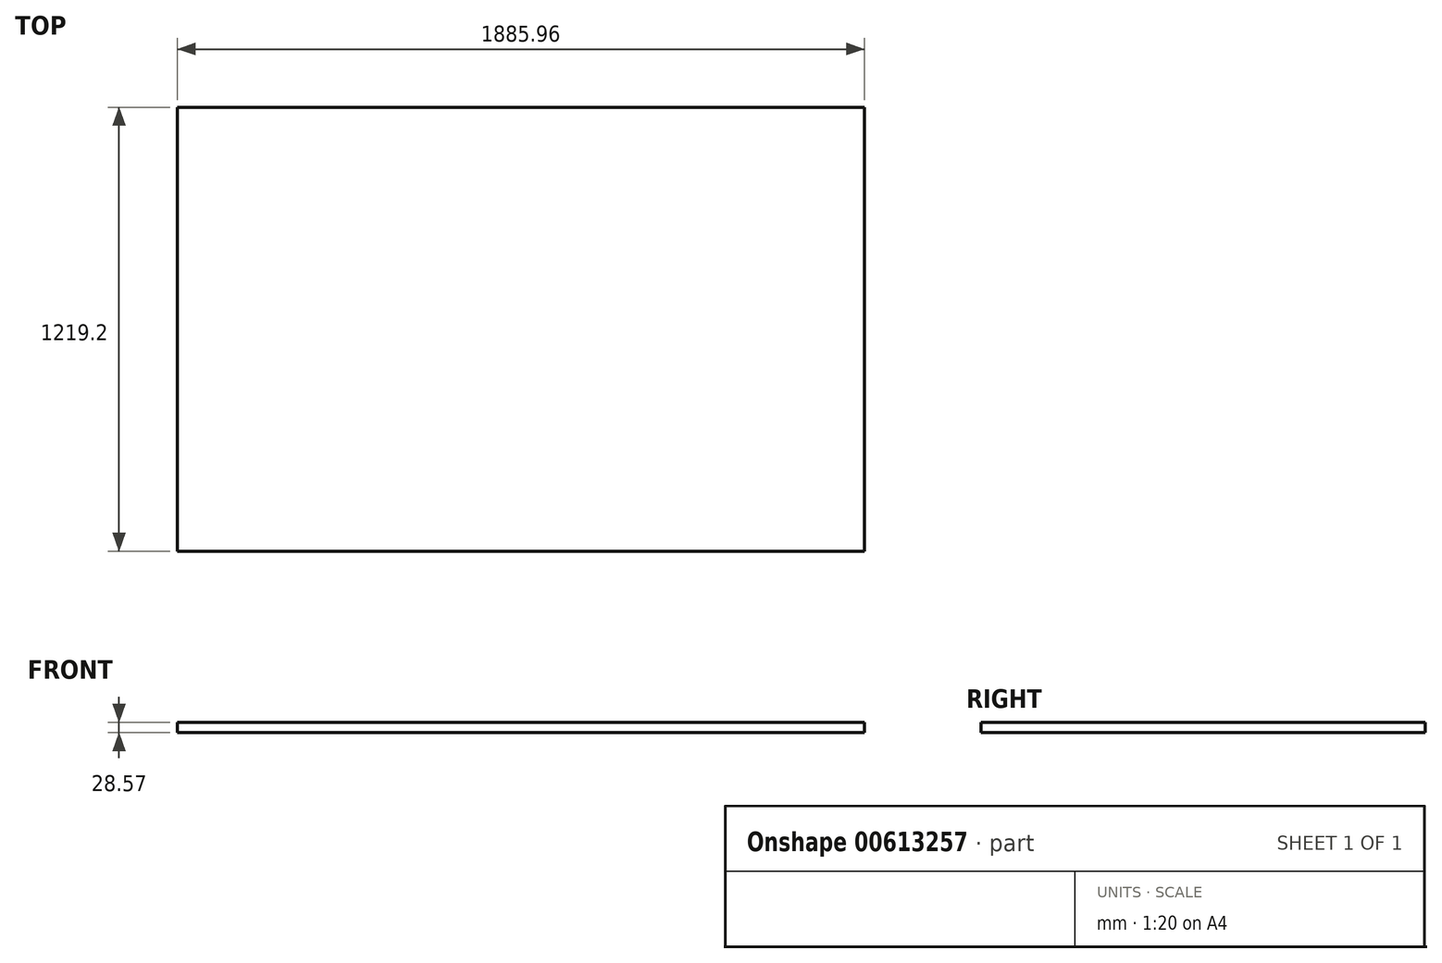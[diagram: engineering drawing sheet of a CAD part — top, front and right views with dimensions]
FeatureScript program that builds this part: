
annotation { "Feature Type Name" : "Feature", "Feature Type Description" : "" }
export const myFeature = defineFeature(function(context is Context, id is Id, definition is map)
    precondition{}
    {
        {
            var Q0;
            Q0=qCreatedBy(makeId("Top.planeOp"),FACE);
            var sketch = newSketch(context, id + "F0", { "sketchPlane" : qUnion([Q0])});
            skLineSegment(sketch, "E0.bottom", {"start": v(942.98, 609.6) * mm, "end": v(-942.98, 609.6) * mm});
            skLineSegment(sketch, "E0.top", {"start": v(942.98, -609.6) * mm, "end": v(-942.98, -609.6) * mm});
            skLineSegment(sketch, "E0.left", {"start": v(942.98, 609.6) * mm, "end": v(942.98, -609.6) * mm});
            skLineSegment(sketch, "E0.right", {"start": v(-942.98, 609.6) * mm, "end": v(-942.98, -609.6) * mm});
            skPoint(sketch, "E0.middle", {"position": v(0, 0) * mm});
            skSolve(sketch);
        }
        {
            var Q0;
            Q0=makeQuery(id+"F0.imprint","IMPRINT",FACE,{"disambiguationData":[TD([[makeQuery(id+"F0.imprint","IMPRINT",EDGE,{"derivedFrom":sQuery(id+"F0.wireOp",EDGE,"E0.bottom")}),1.0]])]});
            extrude(context, id + "F1", {"entities" : qUnion([Q0]), "depth" : 28.57 * mm, "offsetDistance" : 25.4 * mm});
        }
    });
